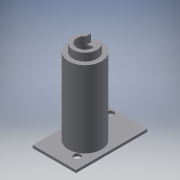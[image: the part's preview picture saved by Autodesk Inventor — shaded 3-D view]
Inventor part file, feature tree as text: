
AUTODESK INVENTOR PART (.ipt)
format: ipt  version: 2016 (Build 200138000, 138)  size: 154,112 bytes
history: native  units: mm
features: sketch x7, extrude x5, projected_geometry x3, loft x1
ambient origin geometry x8: Origin, YZ Plane, XZ Plane, XY Plane, X Axis, Y Axis, Z Axis, Center Point
bodies: Solid1 (feature_tree)
feature tree (16):
  extrude  "Extrusion1"  Depth=28.0mm
  extrude  "Extrusion2"  Depth=1.0mm
  extrude  "Extrusion3"  Depth=4.5mm
  loft  "Loft1"
  extrude  "Extrusion6"  Depth=1.0mm TaperAngle=0.0deg
  extrude  "Extrusion7"  Depth=12.047mm
  sketch  "Sketch1"  dims[d0=17.0mm d1=28.0mm]
  sketch  "Sketch2"  dims[d2=1.0mm d3=0.0mm d4=2.7mm]
  sketch  "Sketch3"  dims[d5=2.7mm d6=4.5mm]
  projected_geometry  "Projected Loop1"
  sketch  "Sketch4"  dims[d7=4.5mm d8=2.0mm]
  projected_geometry  "Projected Loop2"
  sketch  "Sketch5"  dims[d9=5.0mm d10=1.0mm d11=0.0mm]
  sketch  "Sketch6"  dims[d12=13.0mm d13=12.047mm]
  sketch  "Sketch7"  dims[d14=30.0mm d15=0.0mm d16=6.5mm d17=10.0mm d22=0.0mm d23=90.0deg d24=0.0mm d25=90.0deg d26=9.5mm d27=3.0mm d28=0.0mm d29=4.0mm d30=2.0mm d31=2.0mm d32=0.0mm]
  projected_geometry  "Projected Loop3"
